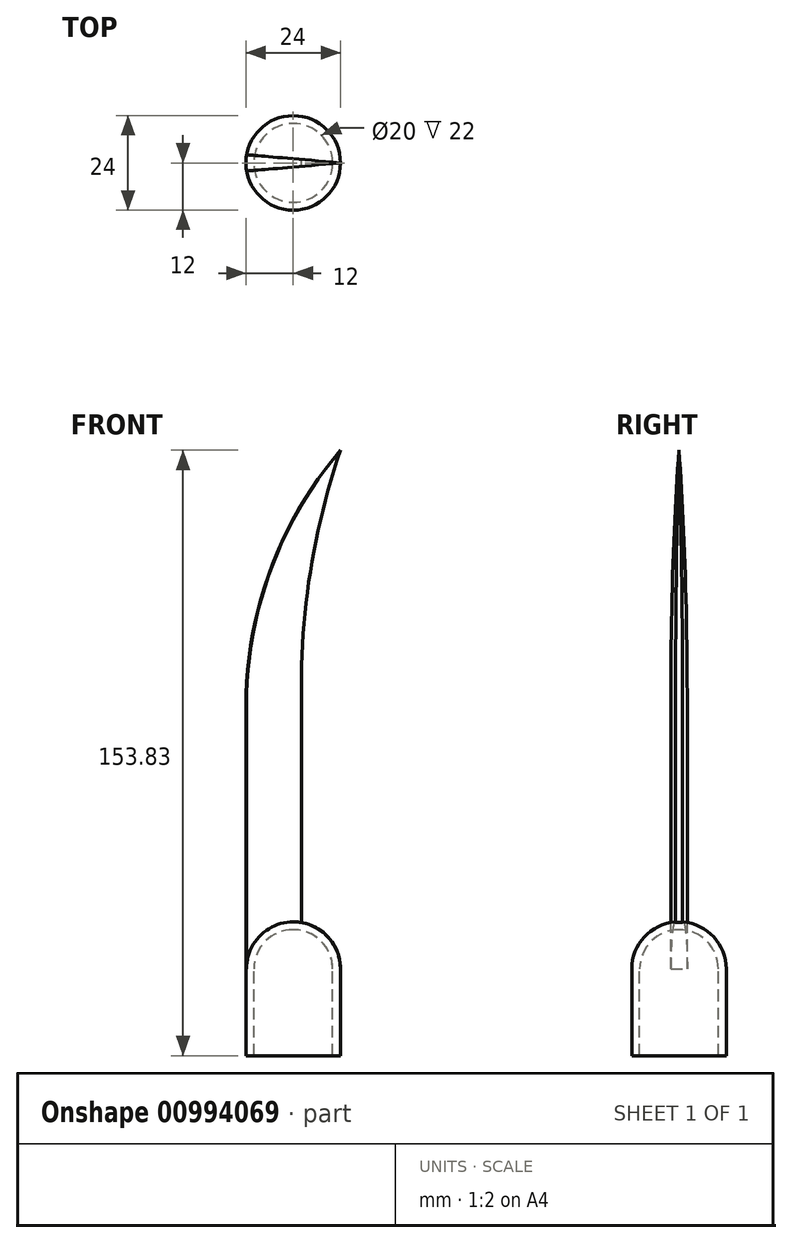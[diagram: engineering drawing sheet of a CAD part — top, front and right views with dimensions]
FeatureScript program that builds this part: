
annotation { "Feature Type Name" : "Feature", "Feature Type Description" : "" }
export const myFeature = defineFeature(function(context is Context, id is Id, definition is map)
    precondition{}
    {
        {
            var Q0;
            Q0=qCreatedBy(makeId("Front.planeOp"),FACE);
            var sketch = newSketch(context, id + "F0", { "sketchPlane" : qUnion([Q0])});
            skLineSegment(sketch, "E0", {"start": v(0, 0) * mm, "end": v(-12, 0) * mm, "construction": true});
            skLineSegment(sketch, "E1", {"start": v(-12, 0) * mm, "end": v(-12, 22) * mm});
            skArc(sketch, "E2", {"start": v(-12, 22) * mm, "mid": v(-8.49, 30.49) * mm, "end": v(0, 34) * mm});
            skLineSegment(sketch, "E3", {"start": v(-12, 0) * mm, "end": v(-10, 0) * mm});
            skLineSegment(sketch, "E4", {"start": v(-10, 0) * mm, "end": v(-10, 22) * mm});
            skArc(sketch, "E5", {"start": v(-10, 22) * mm, "mid": v(-7.07, 29.07) * mm, "end": v(0, 32) * mm});
            skLineSegment(sketch, "E6", {"start": v(0, 32) * mm, "end": v(0, 34) * mm});
            skLineSegment(sketch, "E7", {"start": v(0, 34) * mm, "end": v(0, 0) * mm});
            skSolve(sketch);
        }
        {
            var Q0;
            Q0 = qSketchRegion(id + "F0", true);
            var Q1;
            Q1=sQuery(id+"F0.wireOp",EDGE,"E7");
            revolve(context, id + "F1", {"surfaceOperationType" : NewSurfaceOperationType.NEW, "entities" : qUnion([Q0]), "axis" : qUnion([Q1]), "revolveType" : RevolveType.FULL});
        }
        {
            var Q0;
            Q0=qCreatedBy(makeId("Front.planeOp"),FACE);
            var sketch = newSketch(context, id + "F2", { "sketchPlane" : qUnion([Q0])});
            skLineSegment(sketch, "E8", {"start": v(-12, 0) * mm, "end": v(-12, 22) * mm});
            skLineSegment(sketch, "E9", {"start": v(12, 22) * mm, "end": v(12, 0) * mm});
            skLineSegment(sketch, "E10", {"start": v(-12, 22) * mm, "end": v(-12, 88.84) * mm});
            skArc(sketch, "E11", {"start": v(-12, 88.84) * mm, "mid": v(-5.8, 123.48) * mm, "end": v(12, 153.83) * mm});
            skArc(sketch, "E12", {"start": v(-12, 22) * mm, "mid": v(-7.75, 31.17) * mm, "end": v(2, 33.83) * mm});
            skArc(sketch, "E13", {"start": v(-12, 22) * mm, "mid": v(0, 34) * mm, "end": v(12, 22) * mm});
            skLineSegment(sketch, "E14", {"start": v(2, 33.83) * mm, "end": v(2, 93.83) * mm});
            skArc(sketch, "E15", {"start": v(2, 93.83) * mm, "mid": v(4.52, 124.25) * mm, "end": v(12, 153.83) * mm});
            skLineSegment(sketch, "E16", {"start": v(12, 22) * mm, "end": v(12, 153.83) * mm, "construction": true});
            skSolve(sketch);
        }
        {
            var Q0;
            Q0 = qSketchRegion(id + "F2", true);
            var Q1;
            Q1=sQuery(id+"F2.wireOp",EDGE,"E16");
            revolve(context, id + "F3", {"operationType" : NewBodyOperationType.ADD, "surfaceOperationType" : NewSurfaceOperationType.NEW, "entities" : qUnion([Q0]), "axis" : qUnion([Q1]), "revolveType" : RevolveType.SYMMETRIC, "angle" : 10 * degree});
        }
    });
